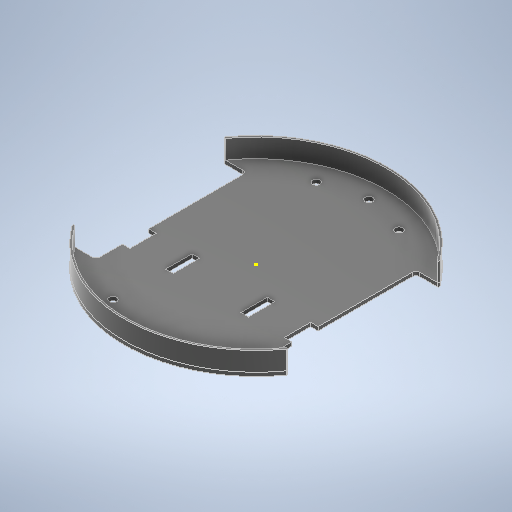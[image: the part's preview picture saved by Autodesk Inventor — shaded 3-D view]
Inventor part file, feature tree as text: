
AUTODESK INVENTOR PART (.ipt)
format: ipt  version: 2025.1 (Build 291241000, 241)  size: 515,072 bytes
history: native  units: mm
features: sketch x3, extrude x2, other x1
ambient origin geometry x8: Origin, YZ Plane, XZ Plane, XY Plane, X Axis, Y Axis, Z Axis, Center Point
bodies: Body1 (feature_tree)
feature tree (6):
  other  "Sólido1"
  extrude  "Extrusão1"  Depth=0.5mm
  sketch  "Esboço2"  dims[d70=138.0mm d71=0.5mm]
  extrude  "Extrusão2"  Depth=0.5mm
  sketch  "Esboço1"  dims[d61=2.0mm d62=0.0mm d69=0.5mm]
  sketch  "Esboço3"  dims[d72=10.0mm d73=0.0mm d76=4.0mm d77=4.0mm d80=4.0mm d81=4.0mm d83=19.0mm d84=14.0mm d86=19.0mm d87=4.0mm d60=0.5mm d63=0.872665mm]
